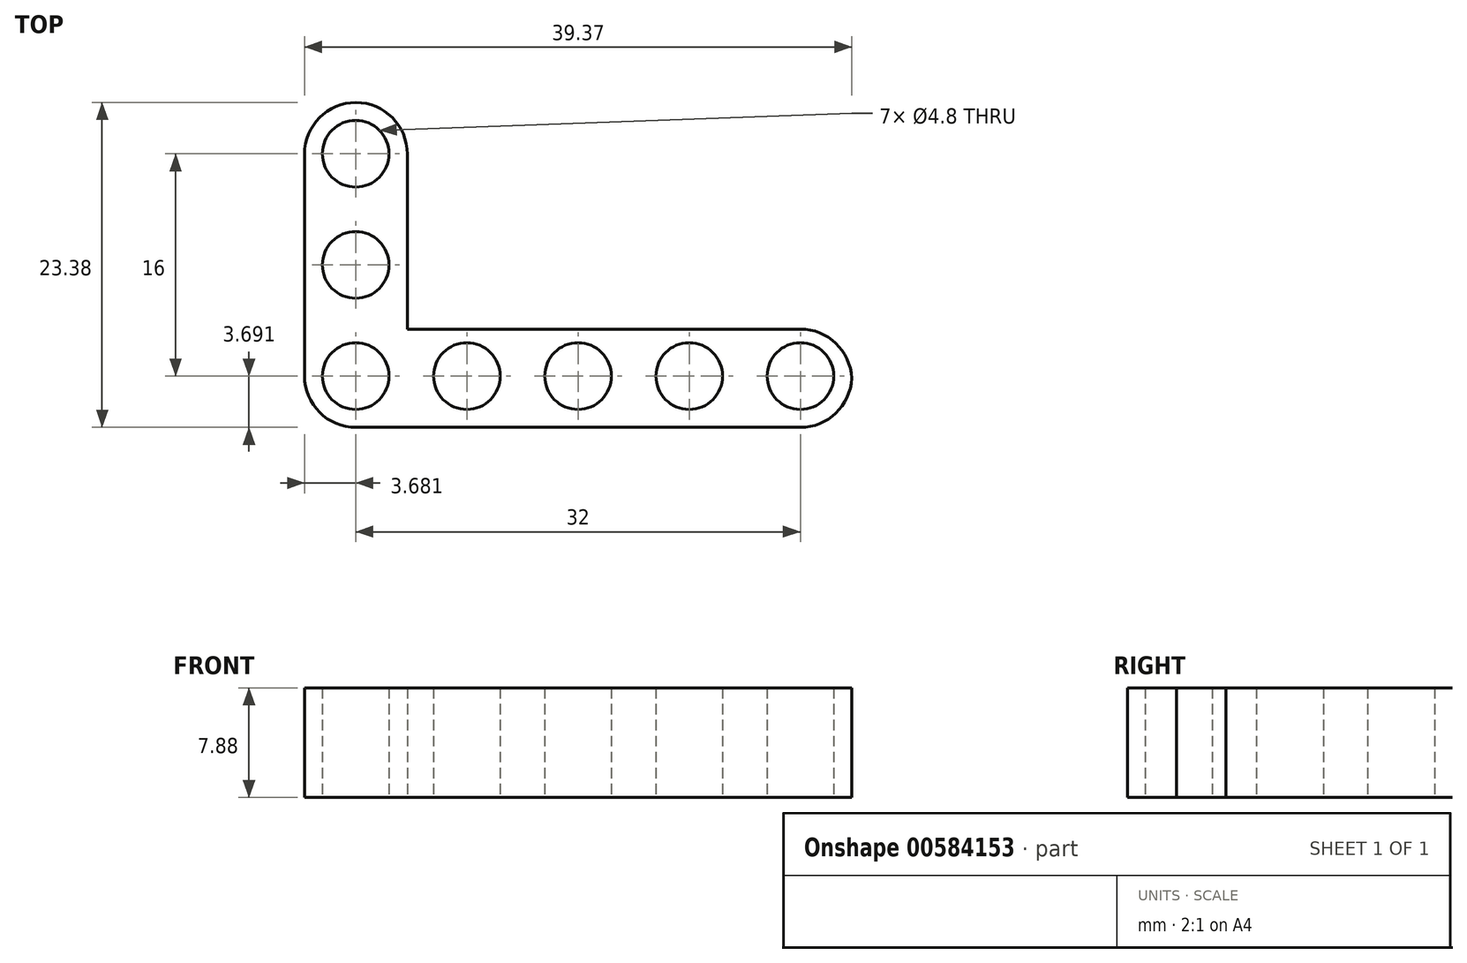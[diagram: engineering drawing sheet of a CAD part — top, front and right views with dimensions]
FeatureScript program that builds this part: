
annotation { "Feature Type Name" : "Feature", "Feature Type Description" : "" }
export const myFeature = defineFeature(function(context is Context, id is Id, definition is map)
    precondition{}
    {
        {
            var Q0;
            Q0=qCreatedBy(makeId("Top.planeOp"),FACE);
            var sketch = newSketch(context, id + "F0", { "sketchPlane" : qUnion([Q0])});
            skLineSegment(sketch, "E0", {"start": v(-28.72, 9.1) * mm, "end": v(-28.72, -19.18) * mm, "construction": true});
            skLineSegment(sketch, "E1", {"start": v(-47.58, -2.09) * mm, "end": v(-47.58, -1.54) * mm, "construction": true});
            skArc(sketch, "E2", {"start": v(-28.72, 0.31) * mm, "mid": v(-31.12, -2.09) * mm, "end": v(-28.72, -4.49) * mm});
            skCircle(sketch, "E3", {"center": v(-36.72, -2.09) * mm, "radius": 2.4 * mm});
            skCircle(sketch, "E4.1.0.0", {"center": v(-44.72, -2.09) * mm, "radius": 2.4 * mm});
            skLineSegment(sketch, "E5.MirrorCS", {"start": v(-31.32, -5.78) * mm, "end": v(-48.4, -5.78) * mm});
            skArc(sketch, "E6.MirrorCS", {"start": v(-28.72, 0.31) * mm, "mid": v(-26.32, -2.09) * mm, "end": v(-28.72, -4.49) * mm});
            skCircle(sketch, "E7", {"center": v(-44.72, 5.91) * mm, "radius": 2.4 * mm});
            skLineSegment(sketch, "E8", {"start": v(-9.03, -5.78) * mm, "end": v(-31.32, -5.78) * mm});
            skCircle(sketch, "E9.0.1.0", {"center": v(-44.72, 13.91) * mm, "radius": 2.4 * mm});
            skLineSegment(sketch, "E9.direction1", {"start": v(-44.72, 5.91) * mm, "end": v(-19.72, 5.91) * mm, "construction": true});
            skLineSegment(sketch, "E9.direction2", {"start": v(-44.72, 5.91) * mm, "end": v(-44.72, 13.91) * mm, "construction": true});
            skArc(sketch, "E10.1.0.0", {"start": v(-20.72, 0.31) * mm, "mid": v(-18.32, -2.09) * mm, "end": v(-20.72, -4.49) * mm});
            skArc(sketch, "E10.1.0.1", {"start": v(-20.72, 0.31) * mm, "mid": v(-23.12, -2.09) * mm, "end": v(-20.72, -4.49) * mm});
            skArc(sketch, "E10.2.0.0", {"start": v(-12.72, 0.31) * mm, "mid": v(-10.32, -2.09) * mm, "end": v(-12.72, -4.49) * mm});
            skArc(sketch, "E10.2.0.1", {"start": v(-12.72, 0.31) * mm, "mid": v(-15.12, -2.09) * mm, "end": v(-12.72, -4.49) * mm});
            skLineSegment(sketch, "E10.direction1", {"start": v(-28.72, -4.49) * mm, "end": v(-20.72, -4.49) * mm, "construction": true});
            skLineSegment(sketch, "E11", {"start": v(-48.4, -5.78) * mm, "end": v(-48.4, 17.6) * mm});
            skLineSegment(sketch, "E12", {"start": v(-48.4, 17.6) * mm, "end": v(-41, 17.6) * mm});
            skLineSegment(sketch, "E13", {"start": v(-41, 17.6) * mm, "end": v(-41, 1.3) * mm});
            skLineSegment(sketch, "E14", {"start": v(-41, 1.3) * mm, "end": v(-9.03, 1.3) * mm});
            skLineSegment(sketch, "E15", {"start": v(-9.03, 1.3) * mm, "end": v(-9.03, -5.78) * mm});
            skSolve(sketch);
        }
        {
            var Q0;
            Q0=makeQuery(id+"F0.imprint","IMPRINT",FACE,{"disambiguationData":[TD([[makeQuery(id+"F0.imprint","IMPRINT",EDGE,{"derivedFrom":sQuery(id+"F0.wireOp",EDGE,"E2")}),-1.0]])]});
            extrude(context, id + "F1", {"entities" : qUnion([Q0]), "depth" : 7.88 * mm, "offsetDistance" : 25 * mm});
        }
        {
            var Q0;
            Q0=makeQuery(id+"F1.opExtrude","SWEPT_EDGE",EDGE,{"disambiguationData":[OSD([sQuery(id+"F0.wireOp",EDGE,"E11"),sQuery(id+"F0.wireOp",EDGE,"E12")])]});
            var Q1;
            Q1=makeQuery(id+"F1.opExtrude","SWEPT_EDGE",EDGE,{"disambiguationData":[OSD([sQuery(id+"F0.wireOp",EDGE,"E12"),sQuery(id+"F0.wireOp",EDGE,"E13")])]});
            var Q2;
            Q2=makeQuery(id+"F1.opExtrude","SWEPT_EDGE",EDGE,{"disambiguationData":[OSD([sQuery(id+"F0.wireOp",EDGE,"E14"),sQuery(id+"F0.wireOp",EDGE,"E15")])]});
            var Q3;
            Q3=makeQuery(id+"F1.opExtrude","SWEPT_EDGE",EDGE,{"disambiguationData":[OSD([sQuery(id+"F0.wireOp",EDGE,"E8"),sQuery(id+"F0.wireOp",EDGE,"E15")])]});
            var Q4;
            Q4=makeQuery(id+"F1.opExtrude","SWEPT_EDGE",EDGE,{"disambiguationData":[OSD([sQuery(id+"F0.wireOp",EDGE,"E5.MirrorCS"),sQuery(id+"F0.wireOp",EDGE,"E11")])]});
            fillet(context, id + "F2", {"entities" : qUnion([Q0, Q1, Q2, Q3, Q4]), "radius" : 3.7 * mm, "tangentPropagation" : true, "allowEdgeOverflow" : false});
        }
    });
